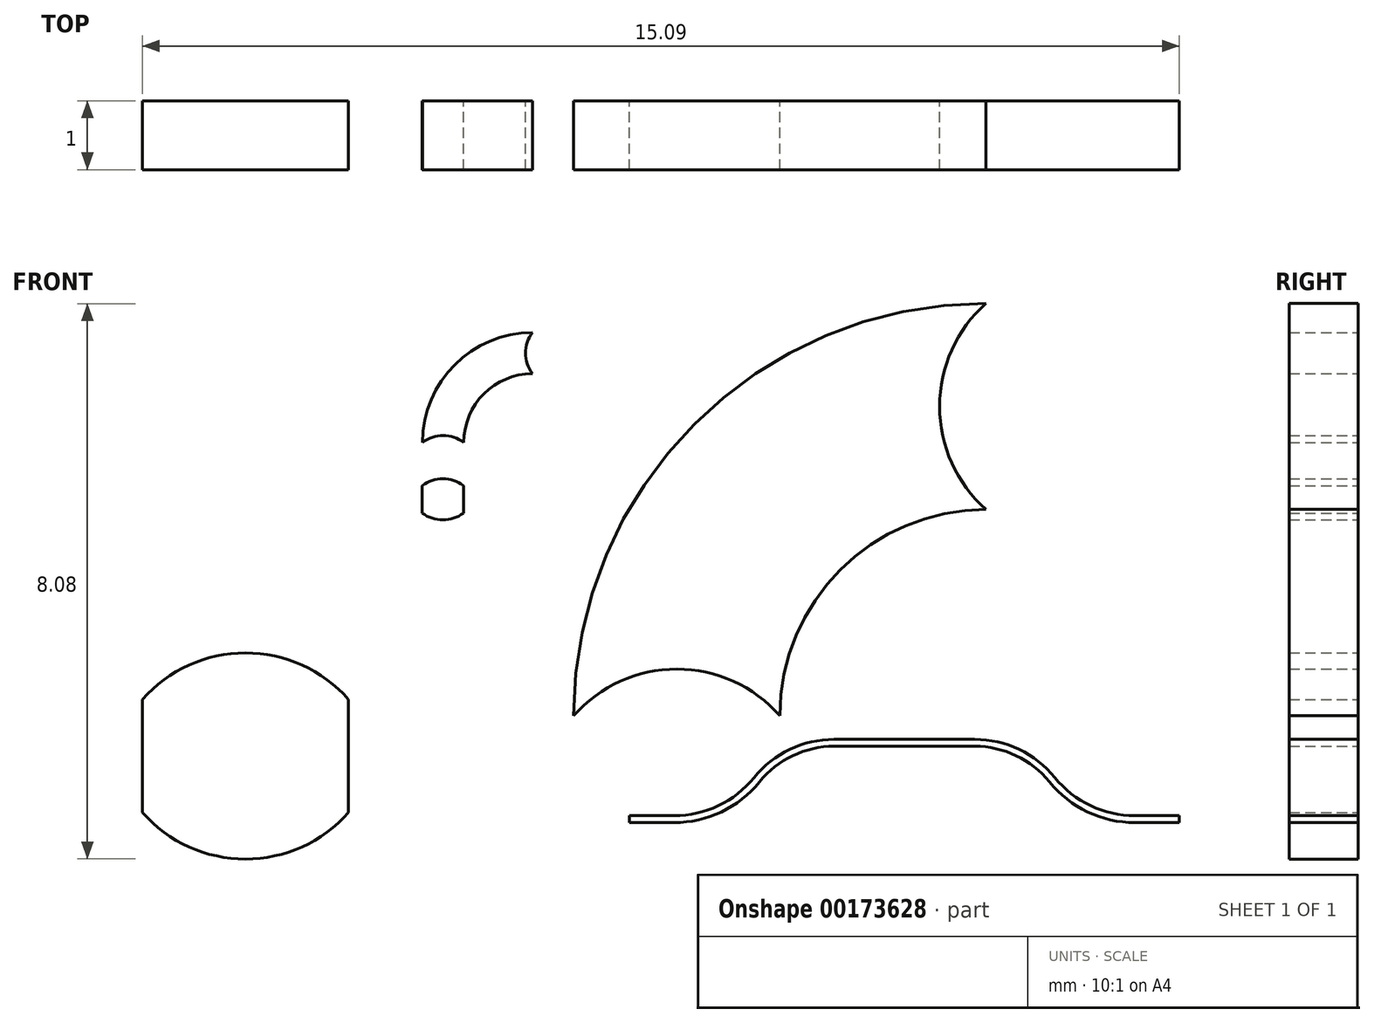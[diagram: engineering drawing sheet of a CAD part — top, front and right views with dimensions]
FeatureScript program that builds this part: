
annotation { "Feature Type Name" : "Feature", "Feature Type Description" : "" }
export const myFeature = defineFeature(function(context is Context, id is Id, definition is map)
    precondition{}
    {
        {
            var Q0;
            Q0=qCreatedBy(makeId("Front.planeOp"),FACE);
            var sketch = newSketch(context, id + "F0", { "sketchPlane" : qUnion([Q0])});
            skLineSegment(sketch, "E0.bottom", {"start": v(-24.42, 2.13) * mm, "end": v(-21.42, 2.13) * mm});
            skLineSegment(sketch, "E0.top", {"start": v(-24.42, 1.3) * mm, "end": v(-21.42, 1.3) * mm});
            skLineSegment(sketch, "E0.left", {"start": v(-24.42, 2.13) * mm, "end": v(-24.42, 1.3) * mm});
            skLineSegment(sketch, "E0.right", {"start": v(-21.42, 2.13) * mm, "end": v(-21.42, 1.3) * mm});
            skArc(sketch, "E1", {"start": v(-24.42, 1.3) * mm, "mid": v(-22.92, 0.63) * mm, "end": v(-21.42, 1.3) * mm});
            skLineSegment(sketch, "E2.MirrorCS", {"start": v(-24.42, 2.95) * mm, "end": v(-21.42, 2.95) * mm});
            skLineSegment(sketch, "E3.MirrorCS", {"start": v(-21.42, 2.13) * mm, "end": v(-21.42, 2.95) * mm});
            skLineSegment(sketch, "E4.MirrorCS", {"start": v(-24.42, 2.13) * mm, "end": v(-24.42, 2.95) * mm});
            skArc(sketch, "E5.MirrorCS", {"start": v(-24.42, 2.95) * mm, "mid": v(-22.92, 3.63) * mm, "end": v(-21.42, 2.95) * mm});
            skLineSegment(sketch, "E6.bottom", {"start": v(-20.35, 5.86) * mm, "end": v(-19.75, 5.86) * mm});
            skLineSegment(sketch, "E6.top", {"start": v(-20.35, 5.66) * mm, "end": v(-19.75, 5.66) * mm});
            skLineSegment(sketch, "E6.left", {"start": v(-20.35, 5.86) * mm, "end": v(-20.35, 5.66) * mm});
            skLineSegment(sketch, "E6.right", {"start": v(-19.75, 5.86) * mm, "end": v(-19.75, 5.66) * mm});
            skArc(sketch, "E7", {"start": v(-20.35, 5.66) * mm, "mid": v(-20.05, 5.56) * mm, "end": v(-19.75, 5.66) * mm});
            skLineSegment(sketch, "E8.MirrorCS", {"start": v(-20.35, 6.06) * mm, "end": v(-19.75, 6.06) * mm});
            skLineSegment(sketch, "E9.MirrorCS", {"start": v(-19.75, 5.86) * mm, "end": v(-19.75, 6.06) * mm});
            skLineSegment(sketch, "E10.MirrorCS", {"start": v(-20.35, 5.86) * mm, "end": v(-20.35, 6.06) * mm});
            skArc(sketch, "E11.MirrorCS", {"start": v(-20.35, 6.06) * mm, "mid": v(-20.05, 6.16) * mm, "end": v(-19.75, 6.06) * mm});
            skArc(sketch, "E12", {"start": v(-12.14, 8.71) * mm, "mid": v(-16.39, 6.96) * mm, "end": v(-18.14, 2.71) * mm});
            skArc(sketch, "E13", {"start": v(-12.14, 5.71) * mm, "mid": v(-14.27, 4.83) * mm, "end": v(-15.14, 2.71) * mm});
            skArc(sketch, "E14", {"start": v(-15.14, 2.71) * mm, "mid": v(-16.64, 3.4) * mm, "end": v(-18.14, 2.71) * mm});
            skArc(sketch, "E15", {"start": v(-12.14, 8.71) * mm, "mid": v(-12.82, 7.21) * mm, "end": v(-12.14, 5.71) * mm});
            skArc(sketch, "E16", {"start": v(-18.74, 8.3) * mm, "mid": v(-19.88, 7.82) * mm, "end": v(-20.34, 6.7) * mm});
            skArc(sketch, "E17", {"start": v(-18.74, 7.7) * mm, "mid": v(-19.45, 7.4) * mm, "end": v(-19.74, 6.7) * mm});
            skArc(sketch, "E18", {"start": v(-19.74, 6.7) * mm, "mid": v(-20.04, 6.8) * mm, "end": v(-20.34, 6.7) * mm});
            skArc(sketch, "E19", {"start": v(-18.74, 8.3) * mm, "mid": v(-18.84, 8) * mm, "end": v(-18.74, 7.7) * mm});
            skSolve(sketch);
        }
        {
            var Q0;
            Q0 = qSketchRegion(id + "F0", true);
            extrude(context, id + "F1", {"entities" : qUnion([Q0]), "depth" : 1 * mm});
        }
        {
            var Q0;
            Q0=qCreatedBy(makeId("Front.planeOp"),FACE);
            var sketch = newSketch(context, id + "F2", { "sketchPlane" : qUnion([Q0])});
            skLineSegment(sketch, "E20.bottom", {"start": v(-17.33, 1.26) * mm, "end": v(-16.68, 1.26) * mm});
            skLineSegment(sketch, "E20.top", {"start": v(-17.33, 1.16) * mm, "end": v(-16.68, 1.16) * mm});
            skLineSegment(sketch, "E20.left", {"start": v(-17.33, 1.26) * mm, "end": v(-17.33, 1.16) * mm});
            skLineSegment(sketch, "E20.right", {"start": v(-16.68, 1.26) * mm, "end": v(-16.68, 1.16) * mm});
            skLineSegment(sketch, "E21.bottom", {"start": v(-14.35, 2.37) * mm, "end": v(-13.33, 2.37) * mm});
            skLineSegment(sketch, "E21.top", {"start": v(-14.35, 2.27) * mm, "end": v(-13.33, 2.27) * mm});
            skLineSegment(sketch, "E21.left", {"start": v(-14.35, 2.37) * mm, "end": v(-14.35, 2.27) * mm});
            skLineSegment(sketch, "E21.right", {"start": v(-13.33, 2.37) * mm, "end": v(-13.33, 2.27) * mm});
            skArc(sketch, "E22", {"start": v(-16.68, 1.26) * mm, "mid": v(-16.04, 1.4) * mm, "end": v(-15.52, 1.81) * mm});
            skArc(sketch, "E23", {"start": v(-14.35, 2.37) * mm, "mid": v(-15, 2.22) * mm, "end": v(-15.52, 1.81) * mm});
            skArc(sketch, "E24", {"start": v(-16.68, 1.16) * mm, "mid": v(-16, 1.31) * mm, "end": v(-15.44, 1.75) * mm});
            skArc(sketch, "E25", {"start": v(-14.35, 2.27) * mm, "mid": v(-14.96, 2.13) * mm, "end": v(-15.44, 1.75) * mm});
            skArc(sketch, "E26.MirrorCS", {"start": v(-9.98, 1.26) * mm, "mid": v(-10.62, 1.4) * mm, "end": v(-11.14, 1.81) * mm});
            skArc(sketch, "E27.MirrorCS", {"start": v(-12.3, 2.37) * mm, "mid": v(-11.66, 2.22) * mm, "end": v(-11.14, 1.81) * mm});
            skLineSegment(sketch, "E28.MirrorCS", {"start": v(-9.33, 1.26) * mm, "end": v(-9.98, 1.26) * mm});
            skLineSegment(sketch, "E29.MirrorCS", {"start": v(-12.3, 2.37) * mm, "end": v(-13.33, 2.37) * mm});
            skArc(sketch, "E30.MirrorCS", {"start": v(-9.98, 1.16) * mm, "mid": v(-10.67, 1.31) * mm, "end": v(-11.22, 1.75) * mm});
            skLineSegment(sketch, "E31.MirrorCS", {"start": v(-12.3, 2.37) * mm, "end": v(-12.3, 2.27) * mm});
            skLineSegment(sketch, "E32.MirrorCS", {"start": v(-9.33, 1.16) * mm, "end": v(-9.98, 1.16) * mm});
            skLineSegment(sketch, "E33.MirrorCS", {"start": v(-9.33, 1.26) * mm, "end": v(-9.33, 1.16) * mm});
            skLineSegment(sketch, "E34.MirrorCS", {"start": v(-9.98, 1.26) * mm, "end": v(-9.98, 1.16) * mm});
            skLineSegment(sketch, "E35.MirrorCS", {"start": v(-12.3, 2.27) * mm, "end": v(-13.33, 2.27) * mm});
            skArc(sketch, "E36.MirrorCS", {"start": v(-12.3, 2.27) * mm, "mid": v(-11.7, 2.13) * mm, "end": v(-11.22, 1.75) * mm});
            skSolve(sketch);
        }
        {
            var Q0;
            Q0 = qSketchRegion(id + "F2", true);
            extrude(context, id + "F3", {"entities" : qUnion([Q0]), "depth" : 1 * mm});
        }
    });
